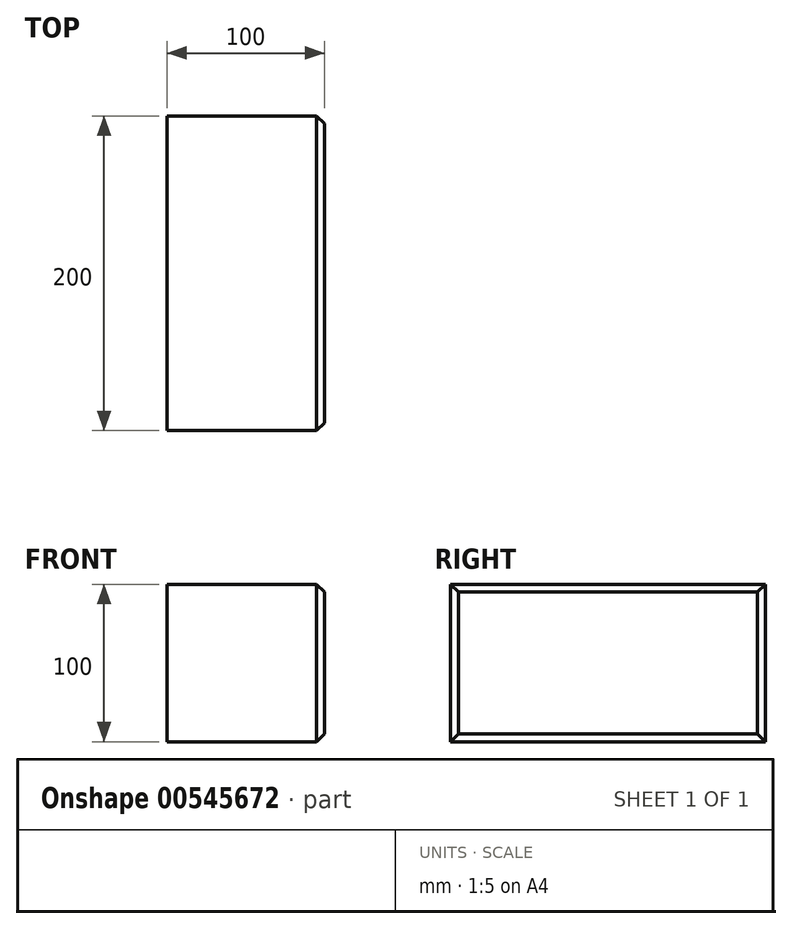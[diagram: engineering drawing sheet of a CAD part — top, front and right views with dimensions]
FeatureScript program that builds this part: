
annotation { "Feature Type Name" : "Feature", "Feature Type Description" : "" }
export const myFeature = defineFeature(function(context is Context, id is Id, definition is map)
    precondition{}
    {
        {
            var Q0;
            Q0=qCreatedBy(makeId("Front.planeOp"),FACE);
            var sketch = newSketch(context, id + "F0", { "sketchPlane" : qUnion([Q0])});
            skLineSegment(sketch, "E0.bottom", {"start": v(-50, 50) * mm, "end": v(50, 50) * mm});
            skLineSegment(sketch, "E0.top", {"start": v(-50, -50) * mm, "end": v(50, -50) * mm});
            skLineSegment(sketch, "E0.left", {"start": v(-50, 50) * mm, "end": v(-50, -50) * mm});
            skLineSegment(sketch, "E0.right", {"start": v(50, 50) * mm, "end": v(50, -50) * mm});
            skSolve(sketch);
        }
        {
            var Q0;
            Q0=makeQuery(id+"F0.imprint","IMPRINT",FACE,{"disambiguationData":[TD([[makeQuery(id+"F0.imprint","IMPRINT",EDGE,{"derivedFrom":sQuery(id+"F0.wireOp",EDGE,"E0.bottom")}),-1.0]])]});
            extrude(context, id + "F1", {"entities" : qUnion([Q0]), "depth" : 100 * mm, "offsetDistance" : 25 * mm});
        }
        {
            var Q0;
            Q0=makeQuery(id+"F1.opExtrude","CAP_FACE",FACE,{"disambiguationData":[OSD([sQuery(id+"F0.wireOp",EDGE,"E0.bottom"),sQuery(id+"F0.wireOp",EDGE,"E0.top"),sQuery(id+"F0.wireOp",EDGE,"E0.left"),sQuery(id+"F0.wireOp",EDGE,"E0.right")])],"isStart":true});
            extrude(context, id + "F2", {"entities" : qUnion([Q0]), "operationType" : NewBodyOperationType.ADD, "depth" : 100 * mm, "offsetDistance" : 25 * mm});
        }
        {
            var Q0;
            {var subQ0=sQuery(id+"F0.wireOp",EDGE,"E0.right");var subQ1=sQuery(id+"F0.wireOp",EDGE,"E0.bottom");Q0=makeQuery(id+"F2.boolean.opBoolean","MERGE",EDGE,{"derivedFrom":[makeQuery(id+"F1.opExtrude","SWEPT_EDGE",EDGE,{"disambiguationData":[OSD([subQ1,subQ0])]}),makeQuery(id+"F2.opExtrude","SWEPT_EDGE",EDGE,{"disambiguationData":[OSD([subQ1,subQ0])]})]});}
            var Q1;
            Q1=makeQuery(id+"F1.opExtrude","CAP_EDGE",EDGE,{"disambiguationData":[OSD([sQuery(id+"F0.wireOp",EDGE,"E0.right")])],"isStart":false});
            var Q2;
            {var subQ0=sQuery(id+"F0.wireOp",EDGE,"E0.right");var subQ1=sQuery(id+"F0.wireOp",EDGE,"E0.top");Q2=makeQuery(id+"F2.boolean.opBoolean","MERGE",EDGE,{"derivedFrom":[makeQuery(id+"F1.opExtrude","SWEPT_EDGE",EDGE,{"disambiguationData":[OSD([subQ1,subQ0])]}),makeQuery(id+"F2.opExtrude","SWEPT_EDGE",EDGE,{"disambiguationData":[OSD([subQ1,subQ0])]})]});}
            var Q3;
            Q3=makeQuery(id+"F2.opExtrude","CAP_EDGE",EDGE,{"disambiguationData":[OSD([sQuery(id+"F0.wireOp",EDGE,"E0.right")])],"isStart":false});
            chamfer(context, id + "F3", {"entities" : qUnion([Q0, Q1, Q2, Q3]), "width" : 5 * mm, "tangentPropagation" : true});
        }
    });
